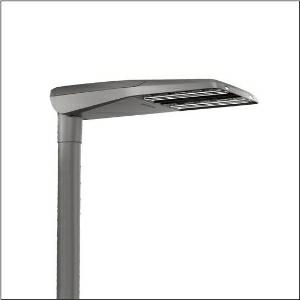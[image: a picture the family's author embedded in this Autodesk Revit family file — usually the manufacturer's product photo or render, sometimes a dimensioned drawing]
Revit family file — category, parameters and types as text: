
# Revit family: streetlight_sl_11_iq_midi___st1_2a_5xc3a41f08le_475e
name_source: partatom
category: Lighting Fixtures
units: mm (PartAtom-declared; Revit-internal decimal feet)

## family parameters
Cut with Voids When Loaded = No
Host = Face
Light Source = No
Part Type = Normal
Room Calculation Point = No
Round Connector Dimension = Use Diameter
Shared = No

## types (1)
- --- (1 x LED, 9590 lm, 60.4 W, 4000K)
    Apparent Load = 60 VA
    CIE Flux Codes = 32 70 96 100 100
    Color Rendering = 70
    Color Temperature = 4000K
    Default Elevation = 1800 mm
    Description = Streetlight SL 11 iQ midi, mast luminaire, primary light control with 3 zone facetted reflector, of plastic, silver coated, highly specular, primary optical cover: cover, of PMMA, transparent, light distribution: ST1.2a, light emission: direct distribution, primary light characteristic: asymmetric, installation type: post-top, side-entry, lamps: LED, High Power LED, rated values: 9.590lm | 60,4W | 158,8lm/W (begin service life); end service life: 9.590lm | 62,5W; at 50% lumin. flux: 4.795lm | 29,7W | 161,4lm/W, colour temperature: 4000K, colour rendering: CRI > 70, light colour: 740, light setting 1 begin service life: 100% | 9.590lm | 60,4W | 158,8lm/W | 4.000K, light setting 1 end service life: 62,5W, further light settings possible, control: Street-Remote, optimised constant luminous flux control (CLO 2.0), Desk-Remote (wireless, voltage-free reading and setting of iQ features in the workshop via application-optimized NFC function/RFID function), Light-Fading, Smart-Wire, Night-Set, Lumen-Switch, Temp-Guard, Auto-Match, with cable H07RN-F 5x 1.5mm², mains connection: 230..240V, AC, 50/60Hz, connection cable pre-assembled, cable length: 8,5m, luminaire housing, of diecast aluminium, powder-coated, Siteco® metallic grey (DB 702S), please order mast flange separately, inclination adjustable without tools: 0°, 5°, 10°, 15° (post-top) | 0°, -5°, -10°, -15° (side-entry), sealing non-destructively replaceable, multi-level sealing system, length: 780mm, width: 376mm, height: 118mm, mast flange for spigot size: 42mm (side-entry): 5XC10008XM4, 60/48mm (side-entry/post-top): 5XC10108XM2, 76/60mm (side-entry/post-top): 5XC10108XM1, equipment: standard, protection rating (complete): IP66, insulation class (complete): insulation class II (safety insulation), certification: CE, ENEC, ENEC+, VDE, impact resistance: IK10, permissible operating ambient temperature for outdoor applications: -25..+50°C, standard-compliant lighting for roads and squares, Environmental Product Declaration (EPD) tested and certified by an independent institute, packaging unit: 1 piece

Light Distribution: ST1.2a
    Height = 118 mm
    Lamp = 1 x LED
    Lamp Light Flux = 9590 lm
    Lamp Power = 60.4 W
    Lamp count = 1
    Length = 780 mm
    Luminous efficacy = 159 lm/W
    Manufacturer = Siteco
    ModVariant = No
    Model = 5XC3A41F08LE
    Number of Poles = 1
    OnlyDefault = Yes
    Power Factor = 1
    Product Name = Streetlight SL 11 iQ midi | ST1.2a
    Product group = mast luminaire | pylon top
    ProductGroupID = 6100
    Protection Class = Protection class II
    Protection Degree = IP 66
    RLX_Detail_Level = 1
    RLX_Emergency_Light_Flux = 0 lm
    RLX_Emergency_Type = 0
    RLX_Emergency_Type_DB = No
    RlxData = <blob elided: 70797 chars, md5=2d100b39>
    Socket = socket
    Standby Power = 0 W
    System Light Flux = 9590 lm
    System Power = 60 W
    Type Comments = factory setting: luminous flux: 100 % | dim-lin: 254 | 520 mA
    Type Image = l_1005960.jpg
    URL = http://relux.com
    VarID = @adj_197016
    Voltage = 0 V
    Weight = 0.00 kg
    Width = 376 mm

## geometry (parser evidence)
native form markers: Blend x4, Sweep x11
no freeform markers — native parametric forms only
